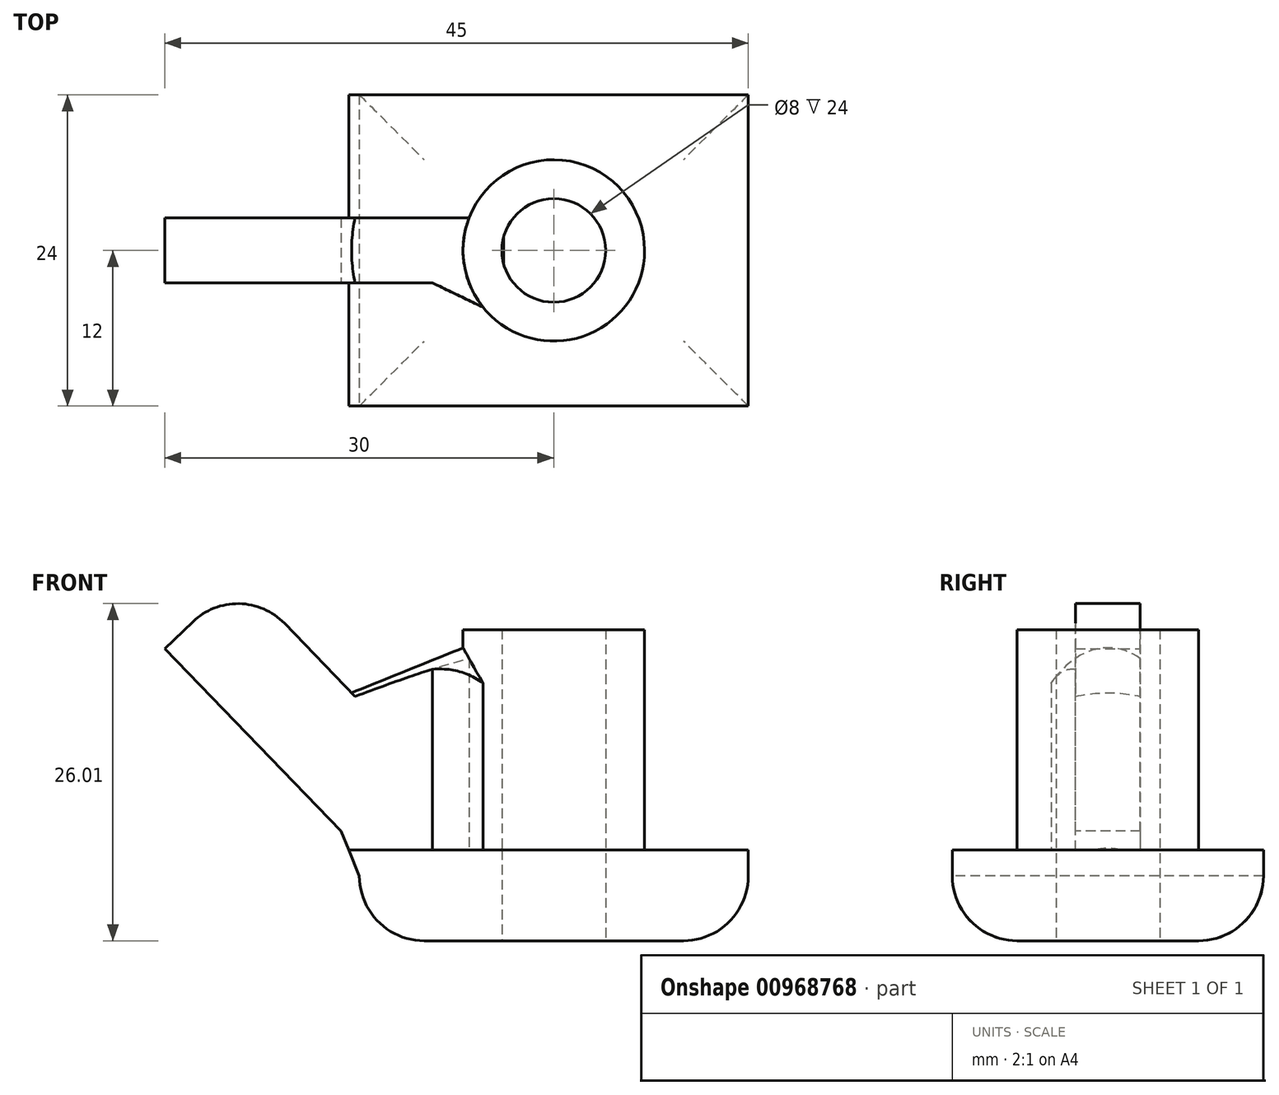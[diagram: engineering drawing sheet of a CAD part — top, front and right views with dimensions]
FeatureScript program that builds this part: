
annotation { "Feature Type Name" : "Feature", "Feature Type Description" : "" }
export const myFeature = defineFeature(function(context is Context, id is Id, definition is map)
    precondition{}
    {
        {
            var Q0;
            Q0=qCreatedBy(makeId("Top.planeOp"),FACE);
            var sketch = newSketch(context, id + "F0", { "sketchPlane" : qUnion([Q0])});
            skLineSegment(sketch, "E0.bottom", {"start": v(-15, 12) * mm, "end": v(15, 12) * mm});
            skLineSegment(sketch, "E0.top", {"start": v(-15, -12) * mm, "end": v(15, -12) * mm});
            skLineSegment(sketch, "E0.left", {"start": v(-15, 12) * mm, "end": v(-15, -12) * mm});
            skLineSegment(sketch, "E0.right", {"start": v(15, 12) * mm, "end": v(15, -12) * mm});
            skPoint(sketch, "E0.middle", {"position": v(0, 0) * mm});
            skSolve(sketch);
        }
        {
            var Q0;
            Q0=makeQuery(id+"F0.imprint","IMPRINT",FACE,{"disambiguationData":[TD([[makeQuery(id+"F0.imprint","IMPRINT",EDGE,{"derivedFrom":sQuery(id+"F0.wireOp",EDGE,"E0.bottom")}),-1.0]])]});
            extrude(context, id + "F1", {"entities" : qUnion([Q0]), "depth" : 7 * mm, "offsetDistance" : 25 * mm});
        }
        {
            var Q0;
            Q0=makeQuery(id+"F1.opExtrude","CAP_FACE",FACE,{"disambiguationData":[OSD([sQuery(id+"F0.wireOp",EDGE,"E0.bottom"),sQuery(id+"F0.wireOp",EDGE,"E0.top"),sQuery(id+"F0.wireOp",EDGE,"E0.left"),sQuery(id+"F0.wireOp",EDGE,"E0.right")])],"isStart":false});
            var sketch = newSketch(context, id + "F2", { "sketchPlane" : qUnion([Q0])});
            skCircle(sketch, "E1", {"center": v(0, 0) * mm, "radius": 7 * mm});
            skCircle(sketch, "E2", {"center": v(0, 0) * mm, "radius": 4 * mm});
            skSolve(sketch);
        }
        {
            var Q0;
            Q0=makeQuery(id+"F2.imprint","IMPRINT",FACE,{"disambiguationData":[TD([[makeQuery(id+"F2.imprint","IMPRINT",EDGE,{"derivedFrom":sQuery(id+"F2.wireOp",EDGE,"E1")}),1.0]])]});
            extrude(context, id + "F3", {"entities" : qUnion([Q0]), "operationType" : NewBodyOperationType.ADD, "depth" : 17 * mm, "offsetDistance" : 25 * mm});
        }
        {
            var Q0;
            Q0=makeQuery(id+"F3.boolean.opBoolean","SPLIT",FACE,{"disambiguationData":[TD([makeQuery(id+"F3.opExtrude","SWEPT_FACE",FACE,{"disambiguationData":[OSD([sQuery(id+"F2.wireOp",EDGE,"E2")])]})])],"derivedFrom":makeQuery(id+"F1.opExtrude","CAP_FACE",FACE,{"disambiguationData":[OSD([sQuery(id+"F0.wireOp",EDGE,"E0.bottom"),sQuery(id+"F0.wireOp",EDGE,"E0.top"),sQuery(id+"F0.wireOp",EDGE,"E0.left"),sQuery(id+"F0.wireOp",EDGE,"E0.right")])],"isStart":false})});
            extrude(context, id + "F4", {"entities" : qUnion([Q0]), "operationType" : NewBodyOperationType.REMOVE, "endBound" : BoundingType.THROUGH_ALL, "oppositeDirection" : true, "depth" : 25 * mm, "offsetDistance" : 25 * mm});
        }
        {
            var Q0;
            Q0=qCreatedBy(makeId("Front.planeOp"),FACE);
            var sketch = newSketch(context, id + "F5", { "sketchPlane" : qUnion([Q0])});
            skLineSegment(sketch, "E3.bottom", {"start": v(0, 0) * mm, "end": v(-30, 0) * mm, "construction": true});
            skLineSegment(sketch, "E3.top", {"start": v(0, 22.52) * mm, "end": v(-30, 22.52) * mm, "construction": true});
            skLineSegment(sketch, "E3.left", {"start": v(0, 0) * mm, "end": v(0, 22.52) * mm, "construction": true});
            skLineSegment(sketch, "E3.right", {"start": v(-30, 0) * mm, "end": v(-30, 22.52) * mm, "construction": true});
            skLineSegment(sketch, "E4.bottom", {"start": v(-30, 0) * mm, "end": v(0, 0) * mm, "construction": true});
            skLineSegment(sketch, "E4.top", {"start": v(-30, 35) * mm, "end": v(0, 35) * mm, "construction": true});
            skLineSegment(sketch, "E4.left", {"start": v(-30, 0) * mm, "end": v(-30, 35) * mm, "construction": true});
            skLineSegment(sketch, "E4.right", {"start": v(0, 0) * mm, "end": v(0, 35) * mm, "construction": true});
            skLineSegment(sketch, "E5", {"start": v(0, 7) * mm, "end": v(-30, 7) * mm, "construction": true});
            skLineSegment(sketch, "E6", {"start": v(-15, 7) * mm, "end": v(-30, 22.52) * mm});
            skLineSegment(sketch, "E7", {"start": v(-30, 22.52) * mm, "end": v(-24.25, 28.08) * mm});
            skLineSegment(sketch, "E8", {"start": v(-24.25, 28.08) * mm, "end": v(-3.87, 7) * mm});
            skLineSegment(sketch, "E9", {"start": v(-3.87, 7) * mm, "end": v(-15, 7) * mm});
            skSolve(sketch);
        }
        {
            var Q0;
            Q0=makeQuery(id+"F5.imprint","IMPRINT",FACE,{"disambiguationData":[TD([[makeQuery(id+"F5.imprint","IMPRINT",EDGE,{"derivedFrom":sQuery(id+"F5.wireOp",EDGE,"E6")}),-1.0]])]});
            extrude(context, id + "F6", {"entities" : qUnion([Q0]), "operationType" : NewBodyOperationType.ADD, "depth" : 2.5 * mm, "offsetDistance" : 25 * mm});
        }
        {
            var Q0;
            Q0=makeQuery(id+"F1.opExtrude","SWEPT_BODY",BODY,{"disambiguationData":[OSD([sQuery(id+"F0.wireOp",EDGE,"E0.bottom"),sQuery(id+"F0.wireOp",EDGE,"E0.top"),sQuery(id+"F0.wireOp",EDGE,"E0.left"),sQuery(id+"F0.wireOp",EDGE,"E0.right")])]});
            var Q1;
            Q1=qCreatedBy(makeId("Front.planeOp"),FACE);
            mirror(context, id + "F7", {"operationType" : NewBodyOperationType.ADD, "entities" : qUnion([Q0]), "mirrorPlane" : qUnion([Q1])});
        }
        {
            var Q0;
            {var subQ0=makeQuery(id+"F6.opExtrude","SWEPT_EDGE",EDGE,{"disambiguationData":[OSD([sQuery(id+"F5.wireOp",EDGE,"E7"),sQuery(id+"F5.wireOp",EDGE,"E8")])]});Q0=makeQuery(id+"F7.boolean.opBoolean","MERGE",EDGE,{"derivedFrom":[subQ0,makeQuery(id+"F7.opPattern","COPY",EDGE,{"derivedFrom":subQ0,"instanceName":"1"})]});}
            var Q1;
            Q1=makeQuery(id+"F1.opExtrude","CAP_EDGE",EDGE,{"disambiguationData":[OSD([sQuery(id+"F0.wireOp",EDGE,"E0.top")])],"isStart":true});
            var Q2;
            Q2=makeQuery(id+"F1.opExtrude","CAP_EDGE",EDGE,{"disambiguationData":[OSD([sQuery(id+"F0.wireOp",EDGE,"E0.left")])],"isStart":true});
            var Q3;
            Q3=makeQuery(id+"F1.opExtrude","CAP_EDGE",EDGE,{"disambiguationData":[OSD([sQuery(id+"F0.wireOp",EDGE,"E0.bottom")])],"isStart":true});
            var Q4;
            Q4=makeQuery(id+"F1.opExtrude","CAP_EDGE",EDGE,{"disambiguationData":[OSD([sQuery(id+"F0.wireOp",EDGE,"E0.right")])],"isStart":true});
            fillet(context, id + "F8", {"entities" : qUnion([Q0, Q1, Q2, Q3, Q4]), "radius" : 5 * mm, "tangentPropagation" : true, "allowEdgeOverflow" : false});
        }
        {
            var Q0;
            {var subQ0=makeQuery(id+"F6.boolean.opBoolean","INTERSECT",EDGE,{"derivedFrom":[makeQuery(id+"F3.opExtrude","SWEPT_FACE",FACE,{"disambiguationData":[OSD([sQuery(id+"F2.wireOp",EDGE,"E1")])]}),makeQuery(id+"F6.opExtrude","SWEPT_FACE",FACE,{"disambiguationData":[OSD([sQuery(id+"F5.wireOp",EDGE,"E8")])]})]});Q0=makeQuery(id+"F7.boolean.opBoolean","MERGE",EDGE,{"derivedFrom":[subQ0,makeQuery(id+"F7.opPattern","COPY",EDGE,{"derivedFrom":subQ0,"instanceName":"1"})]});}
            var Q1;
            Q1=makeQuery(id+"F7.opPattern","COPY",EDGE,{"derivedFrom":makeQuery(id+"F6.boolean.opBoolean","INTERSECT",EDGE,{"derivedFrom":[makeQuery(id+"F3.opExtrude","SWEPT_FACE",FACE,{"disambiguationData":[OSD([sQuery(id+"F2.wireOp",EDGE,"E1")])]}),makeQuery(id+"F6.opExtrude","CAP_FACE",FACE,{"disambiguationData":[OSD([sQuery(id+"F5.wireOp",EDGE,"E6"),sQuery(id+"F5.wireOp",EDGE,"E7"),sQuery(id+"F5.wireOp",EDGE,"E8"),sQuery(id+"F5.wireOp",EDGE,"E9")])],"isStart":false})]}),"instanceName":"1"});
            var Q2;
            Q2=makeQuery(id+"F6.boolean.opBoolean","INTERSECT",EDGE,{"derivedFrom":[makeQuery(id+"F3.opExtrude","SWEPT_FACE",FACE,{"disambiguationData":[OSD([sQuery(id+"F2.wireOp",EDGE,"E1")])]}),makeQuery(id+"F6.opExtrude","CAP_FACE",FACE,{"disambiguationData":[OSD([sQuery(id+"F5.wireOp",EDGE,"E6"),sQuery(id+"F5.wireOp",EDGE,"E7"),sQuery(id+"F5.wireOp",EDGE,"E8"),sQuery(id+"F5.wireOp",EDGE,"E9")])],"isStart":false})]});
            var Q3;
            Q3=makeQuery(id+"F3.opExtrude","CAP_EDGE",EDGE,{"disambiguationData":[OSD([sQuery(id+"F2.wireOp",EDGE,"E1")])],"isStart":true});
            var Q4;
            {var subQ0=sQuery(id+"F5.wireOp",EDGE,"E9");var subQ1=sQuery(id+"F5.wireOp",EDGE,"E6");var subQ2=sQuery(id+"F0.wireOp",EDGE,"E0.left");var subQ3=makeQuery(id+"F1.opExtrude","CAP_EDGE",EDGE,{"disambiguationData":[OSD([subQ2])],"isStart":false});var subQ4=makeQuery(id+"F6.boolean.opBoolean","MERGE",EDGE,{"derivedFrom":[subQ3,makeQuery(id+"F6.opExtrude","SWEPT_EDGE",EDGE,{"disambiguationData":[OSD([subQ1,subQ0])]})]});var subQ5=sQuery(id+"F0.wireOp",EDGE,"E0.bottom");Q4=makeQuery(id+"F7.boolean.opBoolean","MERGE",EDGE,{"derivedFrom":[subQ4,makeQuery(id+"F6.boolean.opBoolean","SPLIT",EDGE,{"disambiguationData":[TD([makeQuery(id+"F1.opExtrude","SWEPT_FACE",FACE,{"disambiguationData":[OSD([subQ5])]})])],"derivedFrom":subQ3}),makeQuery(id+"F7.opPattern","COPY",EDGE,{"derivedFrom":subQ4,"instanceName":"1"})]});}
            var Q5;
            Q5=makeQuery(id+"F6.opExtrude","CAP_EDGE",EDGE,{"disambiguationData":[OSD([sQuery(id+"F5.wireOp",EDGE,"E9")])],"isStart":false});
            var Q6;
            Q6=makeQuery(id+"F7.opPattern","COPY",EDGE,{"derivedFrom":makeQuery(id+"F6.opExtrude","CAP_EDGE",EDGE,{"disambiguationData":[OSD([sQuery(id+"F5.wireOp",EDGE,"E9")])],"isStart":false}),"instanceName":"1"});
            chamfer(context, id + "F9", {"entities" : qUnion([Q0, Q1, Q2, Q3, Q4, Q5, Q6]), "width" : 5 * mm, "tangentPropagation" : true});
        }
    });
